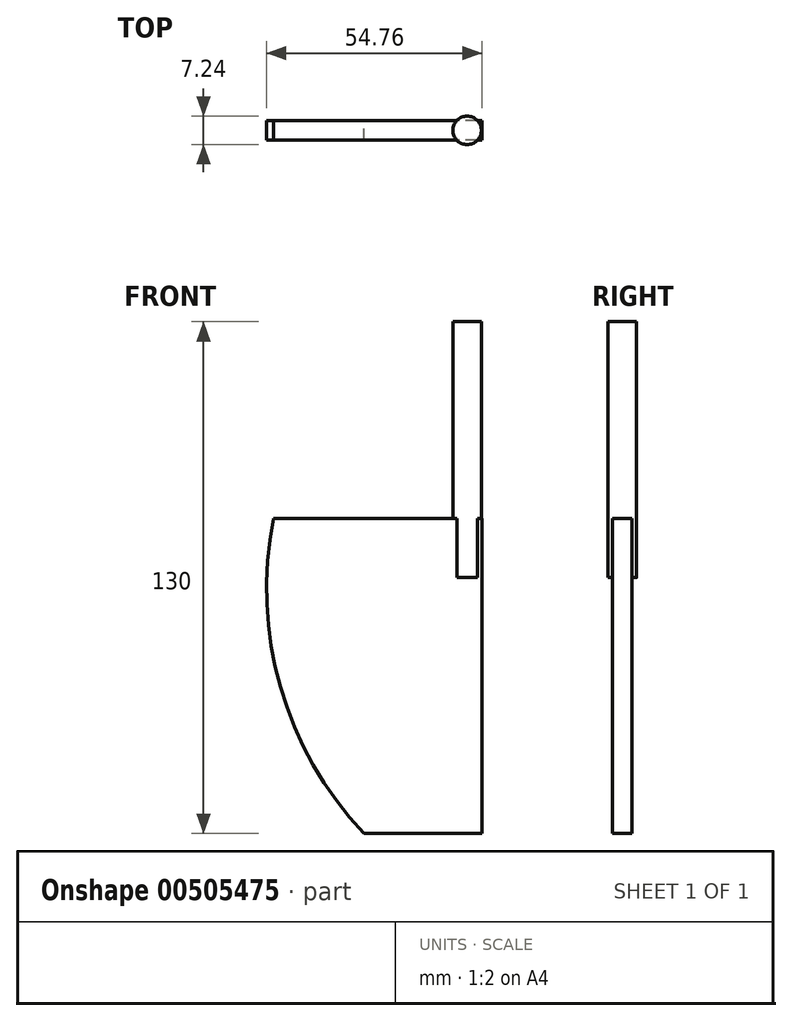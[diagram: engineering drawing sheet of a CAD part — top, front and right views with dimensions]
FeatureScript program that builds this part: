
annotation { "Feature Type Name" : "Feature", "Feature Type Description" : "" }
export const myFeature = defineFeature(function(context is Context, id is Id, definition is map)
    precondition{}
    {
        {
            var Q0;
            Q0=qCreatedBy(makeId("Front.planeOp"),FACE);
            var sketch = newSketch(context, id + "F0", { "sketchPlane" : qUnion([Q0])});
            skLineSegment(sketch, "E0", {"start": v(0, 38.69) * mm, "end": v(0, -41.31) * mm});
            skLineSegment(sketch, "E1", {"start": v(0, -41.31) * mm, "end": v(-30, -41.31) * mm});
            skLineSegment(sketch, "E2", {"start": v(0, 38.69) * mm, "end": v(-53, 38.69) * mm});
            skArc(sketch, "E3", {"start": v(-53, 38.69) * mm, "mid": v(-51.23, -4.1) * mm, "end": v(-30, -41.31) * mm});
            skSolve(sketch);
        }
        {
            var Q0;
            Q0=makeQuery(id+"F0.imprint","IMPRINT",FACE,{"disambiguationData":[TD([[makeQuery(id+"F0.imprint","IMPRINT",EDGE,{"derivedFrom":sQuery(id+"F0.wireOp",EDGE,"E0")}),-1.0]])]});
            extrude(context, id + "F1", {"entities" : qUnion([Q0]), "depth" : 5 * mm});
        }
        {
            var Q0;
            Q0=makeQuery(id+"F1.opExtrude","SWEPT_FACE",FACE,{"disambiguationData":[OSD([sQuery(id+"F0.wireOp",EDGE,"E2")])]});
            var sketch = newSketch(context, id + "F2", { "sketchPlane" : qUnion([Q0])});
            skCircle(sketch, "E4", {"center": v(-3.78, -2.5) * mm, "radius": 3.62 * mm});
            skPoint(sketch, "E4.centerSnap0", {"position": v(0, -2.5) * mm});
            skSolve(sketch);
        }
        {
            var Q0;
            {var subQ0=sQuery(id+"F2.wireOp",EDGE,"E4");var subQ1=makeQuery(id+"F1.opExtrude","CAP_EDGE",EDGE,{"disambiguationData":[OSD([sQuery(id+"F0.wireOp",EDGE,"E2")])],"isStart":true});var subQ2=makeQuery(id+"F2.imprint","INTERSECT",VERTEX,{"disambiguationData":[OD(0.0)],"derivedFrom":[subQ1,subQ0]});Q0=makeQuery(id+"F2.imprint","IMPRINT",FACE,{"disambiguationData":[TD([[makeQuery(id+"F2.imprint","IMPRINT",EDGE,{"disambiguationData":[TD([[subQ2,1.0]])],"derivedFrom":subQ0}),1.0]])]});}
            var Q1;
            {var subQ0=sQuery(id+"F2.wireOp",EDGE,"E4");var subQ1=makeQuery(id+"F1.opExtrude","CAP_EDGE",EDGE,{"disambiguationData":[OSD([sQuery(id+"F0.wireOp",EDGE,"E2")])],"isStart":false});var subQ2=makeQuery(id+"F2.imprint","INTERSECT",VERTEX,{"disambiguationData":[OD(0.0)],"derivedFrom":[subQ1,subQ0]});Q1=makeQuery(id+"F2.imprint","IMPRINT",FACE,{"disambiguationData":[TD([[makeQuery(id+"F2.imprint","IMPRINT",EDGE,{"disambiguationData":[TD([[subQ2,-1.0]])],"derivedFrom":subQ0}),1.0]])]});}
            extrude(context, id + "F3", {"entities" : qUnion([Q0, Q1]), "operationType" : NewBodyOperationType.ADD, "oppositeDirection" : true, "depth" : 15 * mm});
        }
        {
            var Q0;
            {var subQ0=sQuery(id+"F2.wireOp",EDGE,"E4");var subQ1=sQuery(id+"F0.wireOp",EDGE,"E2");var subQ2=makeQuery(id+"F1.opExtrude","CAP_EDGE",EDGE,{"disambiguationData":[OSD([subQ1])],"isStart":true});var subQ3=makeQuery(id+"F2.imprint","INTERSECT",VERTEX,{"disambiguationData":[OD(0.0)],"derivedFrom":[subQ2,subQ0]});Q0=makeQuery(id+"F2.imprint","IMPRINT",FACE,{"disambiguationData":[TD([[makeQuery(id+"F2.imprint","IMPRINT",EDGE,{"disambiguationData":[TD([[subQ3,-1.0]])],"derivedFrom":subQ0}),1.0]])]});}
            var Q1;
            {var subQ0=sQuery(id+"F2.wireOp",EDGE,"E4");var subQ1=makeQuery(id+"F1.opExtrude","CAP_EDGE",EDGE,{"disambiguationData":[OSD([sQuery(id+"F0.wireOp",EDGE,"E2")])],"isStart":true});var subQ2=makeQuery(id+"F2.imprint","INTERSECT",VERTEX,{"disambiguationData":[OD(0.0)],"derivedFrom":[subQ1,subQ0]});Q1=makeQuery(id+"F2.imprint","IMPRINT",FACE,{"disambiguationData":[TD([[makeQuery(id+"F2.imprint","IMPRINT",EDGE,{"disambiguationData":[TD([[subQ2,1.0]])],"derivedFrom":subQ0}),1.0]])]});}
            var Q2;
            {var subQ0=sQuery(id+"F2.wireOp",EDGE,"E4");var subQ1=makeQuery(id+"F1.opExtrude","CAP_EDGE",EDGE,{"disambiguationData":[OSD([sQuery(id+"F0.wireOp",EDGE,"E2")])],"isStart":false});var subQ2=makeQuery(id+"F2.imprint","INTERSECT",VERTEX,{"disambiguationData":[OD(0.0)],"derivedFrom":[subQ1,subQ0]});Q2=makeQuery(id+"F2.imprint","IMPRINT",FACE,{"disambiguationData":[TD([[makeQuery(id+"F2.imprint","IMPRINT",EDGE,{"disambiguationData":[TD([[subQ2,-1.0]])],"derivedFrom":subQ0}),1.0]])]});}
            extrude(context, id + "F4", {"entities" : qUnion([Q0, Q1, Q2]), "operationType" : NewBodyOperationType.ADD, "depth" : 50 * mm});
        }
    });
